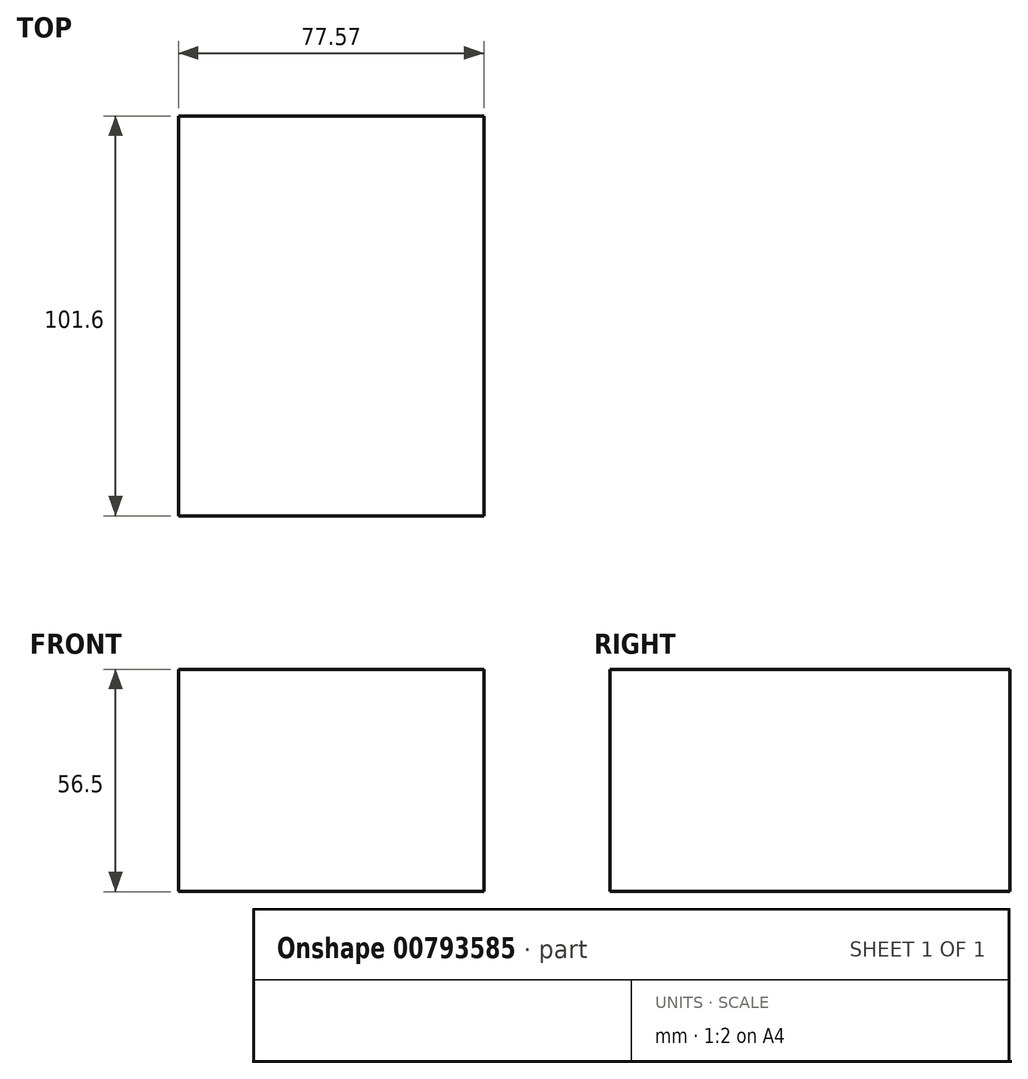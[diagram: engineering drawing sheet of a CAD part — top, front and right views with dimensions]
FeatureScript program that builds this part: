
annotation { "Feature Type Name" : "Feature", "Feature Type Description" : "" }
export const myFeature = defineFeature(function(context is Context, id is Id, definition is map)
    precondition{}
    {
        {
            var Q0;
            Q0=qCreatedBy(makeId("Front.planeOp"),FACE);
            var sketch = newSketch(context, id + "F0", { "sketchPlane" : qUnion([Q0])});
            skLineSegment(sketch, "E0.bottom", {"start": v(-31.6, 17.56) * mm, "end": v(45.96, 17.56) * mm});
            skLineSegment(sketch, "E0.top", {"start": v(-31.6, -38.94) * mm, "end": v(45.96, -38.94) * mm});
            skLineSegment(sketch, "E0.left", {"start": v(-31.6, 17.56) * mm, "end": v(-31.6, -38.94) * mm});
            skLineSegment(sketch, "E0.right", {"start": v(45.96, 17.56) * mm, "end": v(45.96, -38.94) * mm});
            skSolve(sketch);
        }
        {
            var Q0;
            Q0=makeQuery(id+"F0.imprint","IMPRINT",FACE,{"disambiguationData":[TD([[makeQuery(id+"F0.imprint","IMPRINT",EDGE,{"derivedFrom":sQuery(id+"F0.wireOp",EDGE,"E0.bottom")}),-1.0]])]});
            extrude(context, id + "F1", {"entities" : qUnion([Q0]), "depth" : 101.6 * mm, "offsetDistance" : 25.4 * mm});
        }
    });
